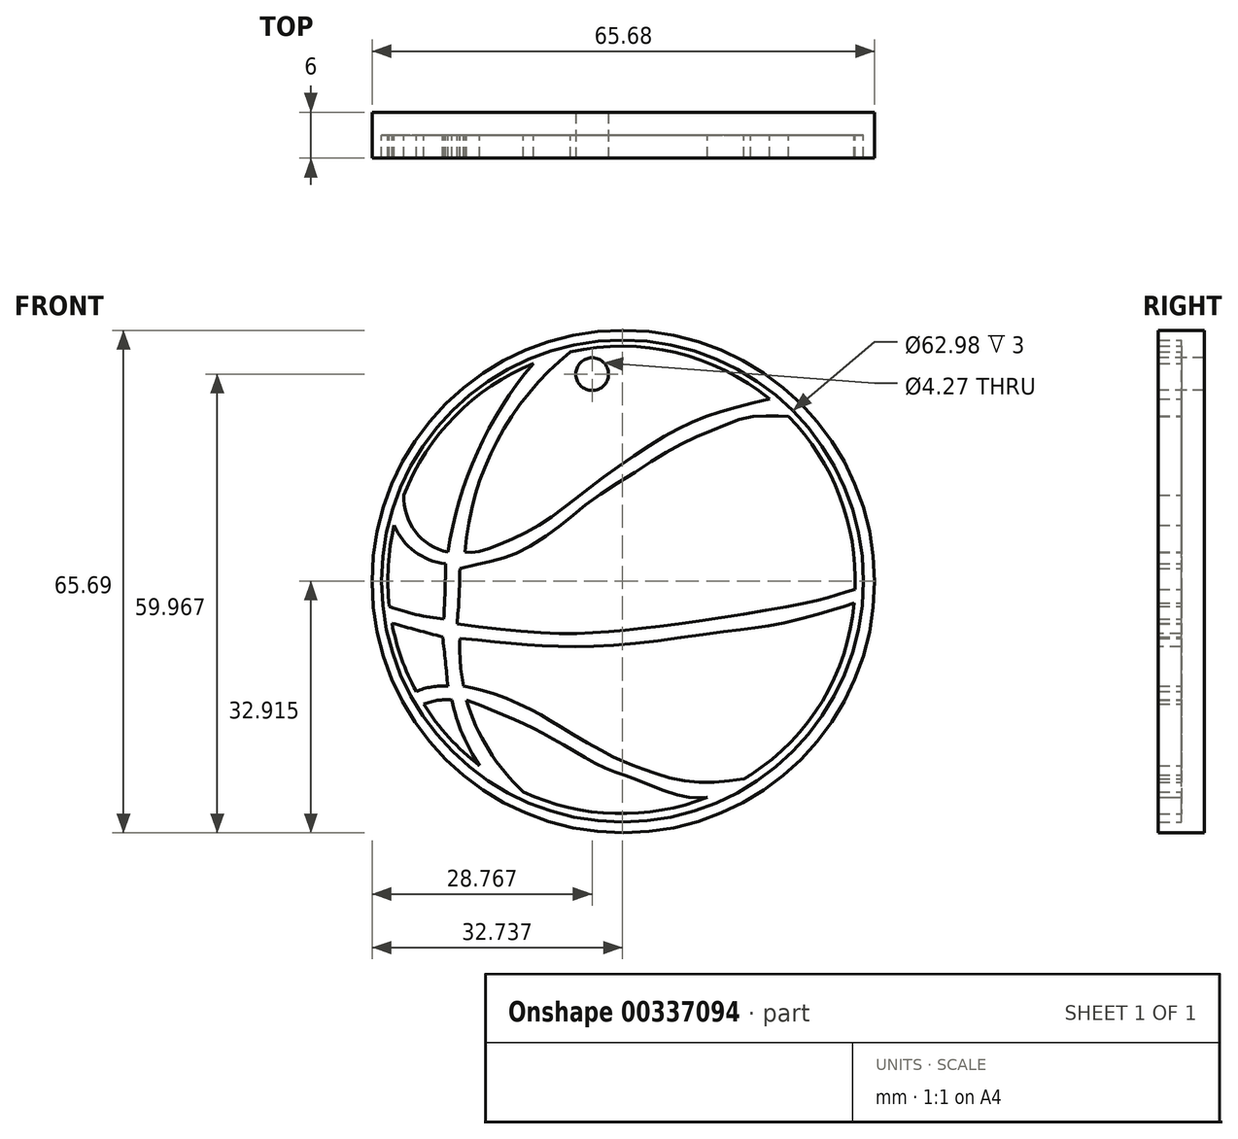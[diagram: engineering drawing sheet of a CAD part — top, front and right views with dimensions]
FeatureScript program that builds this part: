
annotation { "Feature Type Name" : "Feature", "Feature Type Description" : "" }
export const myFeature = defineFeature(function(context is Context, id is Id, definition is map)
    precondition{}
    {
        {
            var Q0;
            Q0=qCreatedBy(makeId("Front.planeOp"),FACE);
            var sketch = newSketch(context, id + "F0", { "sketchPlane" : qUnion([Q0])});
            skCircle(sketch, "E0", {"center": v(1.45, 1.07) * mm, "radius": 31.49 * mm});
            skPoint(sketch, "E0.first.point", {"position": v(-24.62, -16.6) * mm});
            skPoint(sketch, "E0.second.point", {"position": v(30.66, 12.8) * mm});
            skPoint(sketch, "E0.third.point", {"position": v(-14.09, 28.45) * mm});
            skFitSpline(sketch, "E1", {"points": [v(-19.8, -6.45) * mm, v(-12.36, -7.12) * mm, v(-6.04, -7.5) * mm, v(4.04, -6.97) * mm, v(15.92, -5.4) * mm, v(21.41, -4.64) * mm, v(28.48, -2.84) * mm, v(31.72, -1.78) * mm], "startDerivative": vector(52.87, -4.89) * mm, "endDerivative": vector(28.74, 9.86) * mm});
            skArc(sketch, "E2", {"start": v(-28.38, 8.36) * mm, "mid": v(-29.17, 3.08) * mm, "end": v(-29.03, -2.26) * mm});
            skPoint(sketch, "E2.first.point", {"position": v(-29.13, -1.18) * mm});
            skPoint(sketch, "E2.second.point", {"position": v(17.43, 27.18) * mm});
            skPoint(sketch, "E2.third.point", {"position": v(18.18, -24.27) * mm});
            skFitSpline(sketch, "E3", {"points": [v(31.85, 0) * mm, v(29.23, -0.8) * mm, v(25.1, -1.86) * mm, v(11.7, -4.11) * mm, v(1.18, -5.4) * mm, v(-7.17, -5.77) * mm, v(-20.18, -4.57) * mm], "startDerivative": vector(-26.82, -8.38) * mm, "endDerivative": vector(-65.54, 7.8) * mm});
            skArc(sketch, "E4", {"start": v(-27.14, 12.31) * mm, "mid": v(-25.62, 7.53) * mm, "end": v(-21.39, 4.84) * mm});
            skArc(sketch, "E5", {"start": v(-28.38, 8.36) * mm, "mid": v(-25.73, 4.91) * mm, "end": v(-21.69, 3.33) * mm});
            skArc(sketch, "E6", {"start": v(-21.39, -12.69) * mm, "mid": v(-23.5, -12.78) * mm, "end": v(-25.52, -13.37) * mm});
            skArc(sketch, "E7", {"start": v(-20.86, -14.5) * mm, "mid": v(-22.74, -14.53) * mm, "end": v(-24.54, -15.04) * mm});
            skArc(sketch, "E8", {"start": v(-28.7, -4.45) * mm, "mid": v(-25.39, -5.36) * mm, "end": v(-22.06, -6.22) * mm});
            skArc(sketch, "E9", {"start": v(-29.03, -2.26) * mm, "mid": v(-25.53, -3.32) * mm, "end": v(-21.91, -3.89) * mm});
            skArc(sketch, "E10", {"start": v(-10.2, 29.5) * mm, "mid": v(-17.52, 17.95) * mm, "end": v(-21.39, 4.84) * mm});
            skArc(sketch, "E11", {"start": v(-21.91, -3.89) * mm, "mid": v(-21.76, -0.28) * mm, "end": v(-21.69, 3.33) * mm});
            skArc(sketch, "E12", {"start": v(-21.39, -12.69) * mm, "mid": v(-21.7, -9.45) * mm, "end": v(-22.06, -6.22) * mm});
            skArc(sketch, "E13", {"start": v(-20.86, -14.5) * mm, "mid": v(-19.46, -18.96) * mm, "end": v(-17.23, -23.06) * mm});
            skArc(sketch, "E14", {"start": v(-18.98, -14.5) * mm, "mid": v(-16.05, -21) * mm, "end": v(-11.5, -26.52) * mm});
            skArc(sketch, "E15", {"start": v(-19.8, -6.45) * mm, "mid": v(-19.75, -9.58) * mm, "end": v(-19.35, -12.69) * mm});
            skArc(sketch, "E16", {"start": v(-20.18, -4.57) * mm, "mid": v(-19.92, -0.92) * mm, "end": v(-19.8, 2.73) * mm});
            skArc(sketch, "E17", {"start": v(-5.37, 31.02) * mm, "mid": v(-14.96, 19.36) * mm, "end": v(-19.16, 4.86) * mm});
            skFitSpline(sketch, "E18", {"points": [v(-19.16, 4.86) * mm, v(-17.73, 4.86) * mm, v(-14.42, 5.94) * mm, v(-8.7, 8.89) * mm, v(-2.61, 13.45) * mm, v(5.88, 19.35) * mm, v(12.6, 22.66) * mm, v(20.7, 24.84) * mm], "startDerivative": vector(18.93, -1.68) * mm, "endDerivative": vector(50.1, 11.47) * mm});
            skFitSpline(sketch, "E19", {"points": [v(23.16, 22.58) * mm, v(20.9, 22.66) * mm, v(17.6, 22.4) * mm, v(13.66, 20.96) * mm, v(8.83, 18.82) * mm, v(3.56, 15.6) * mm, v(-2.88, 11.4) * mm, v(-6.82, 8.17) * mm, v(-12.1, 4.86) * mm, v(-15.14, 3.79) * mm, v(-19.8, 2.73) * mm], "startDerivative": vector(-30.82, 1.74) * mm, "endDerivative": vector(-49.79, -10.77) * mm});
            skFitSpline(sketch, "E20", {"points": [v(-19.35, -12.69) * mm, v(-15.94, -13.47) * mm, v(-10.58, -15.71) * mm, v(-6.73, -17.95) * mm, v(0, -21.8) * mm, v(3.56, -23.31) * mm, v(9.9, -25.1) * mm, v(17.32, -24.82) * mm], "startDerivative": vector(27.74, -4.94) * mm, "endDerivative": vector(44.65, 5.64) * mm});
            skFitSpline(sketch, "E21", {"points": [v(-18.98, -14.5) * mm, v(-16.93, -15.26) * mm, v(-12.45, -17.14) * mm, v(-9.14, -18.75) * mm, v(-4.85, -21.17) * mm, v(-0.83, -23.4) * mm, v(3.1, -24.83) * mm, v(9.37, -27.07) * mm, v(12.57, -27.2) * mm], "startDerivative": vector(20.02, -7.25) * mm, "endDerivative": vector(26.35, 2.3) * mm});
            skArc(sketch, "E22.trimOffspring", {"start": v(-28.7, -4.45) * mm, "mid": v(-27.46, -9.03) * mm, "end": v(-25.52, -13.37) * mm});
            skArc(sketch, "E23.trimOffspring", {"start": v(-24.54, -15.04) * mm, "mid": v(-21.24, -19.38) * mm, "end": v(-17.23, -23.06) * mm});
            skArc(sketch, "E24.trimOffspring", {"start": v(-11.5, -26.52) * mm, "mid": v(0.46, -29.33) * mm, "end": v(12.57, -27.2) * mm});
            skArc(sketch, "E25.trimOffspring", {"start": v(17.32, -24.82) * mm, "mid": v(17.75, -24.55) * mm, "end": v(18.18, -24.27) * mm});
            skArc(sketch, "E26.trimOffspring", {"start": v(20.7, 24.84) * mm, "mid": v(8.38, 30.94) * mm, "end": v(-5.37, 31.02) * mm});
            skArc(sketch, "E27.trimOffspring", {"start": v(-10.2, 29.5) * mm, "mid": v(-20.44, 22.65) * mm, "end": v(-27.14, 12.31) * mm});
            skArc(sketch, "E28.trimOffspring", {"start": v(31.85, 0) * mm, "mid": v(29.84, 12.19) * mm, "end": v(23.16, 22.58) * mm});
            skFitSpline(sketch, "E29", {"points": [v(31.72, -1.78) * mm, v(33.97, -1.04) * mm], "startDerivative": vector(2.25, 0.74) * mm, "endDerivative": vector(2.25, 0.74) * mm});
            skArc(sketch, "E30", {"start": v(18.18, -24.27) * mm, "mid": v(27.58, -14.6) * mm, "end": v(31.72, -1.78) * mm});
            skCircle(sketch, "E31", {"center": v(1.55, 1) * mm, "radius": 32.84 * mm});
            skPoint(sketch, "E31.first.point", {"position": v(-29.62, -9.36) * mm});
            skPoint(sketch, "E31.second.point", {"position": v(24.95, 24.04) * mm});
            skPoint(sketch, "E31.third.point", {"position": v(25.6, -21.38) * mm});
            skSolve(sketch);
        }
        {
            var Q0;
            Q0=makeQuery(id+"F0.imprint","IMPRINT",FACE,{"disambiguationData":[TD([[makeQuery(id+"F0.imprint","IMPRINT",EDGE,{"derivedFrom":sQuery(id+"F0.wireOp",EDGE,"E3")}),-1.0]])]});
            var Q1;
            Q1=makeQuery(id+"F0.imprint","IMPRINT",FACE,{"disambiguationData":[TD([[makeQuery(id+"F0.imprint","IMPRINT",EDGE,{"derivedFrom":sQuery(id+"F0.wireOp",EDGE,"E17")}),1.0]])]});
            var Q2;
            Q2=makeQuery(id+"F0.imprint","IMPRINT",FACE,{"disambiguationData":[TD([[makeQuery(id+"F0.imprint","IMPRINT",EDGE,{"derivedFrom":sQuery(id+"F0.wireOp",EDGE,"E0")}),1.0]])]});
            var Q3;
            Q3=makeQuery(id+"F0.imprint","IMPRINT",FACE,{"disambiguationData":[TD([[makeQuery(id+"F0.imprint","IMPRINT",EDGE,{"derivedFrom":sQuery(id+"F0.wireOp",EDGE,"E1")}),-1.0]])]});
            var Q4;
            Q4=makeQuery(id+"F0.imprint","IMPRINT",FACE,{"disambiguationData":[TD([[makeQuery(id+"F0.imprint","IMPRINT",EDGE,{"derivedFrom":sQuery(id+"F0.wireOp",EDGE,"E6")}),-1.0]])]});
            var Q5;
            Q5=makeQuery(id+"F0.imprint","IMPRINT",FACE,{"disambiguationData":[TD([[makeQuery(id+"F0.imprint","IMPRINT",EDGE,{"derivedFrom":sQuery(id+"F0.wireOp",EDGE,"E14")}),1.0]])]});
            var Q6;
            Q6=makeQuery(id+"F0.imprint","IMPRINT",FACE,{"disambiguationData":[TD([[makeQuery(id+"F0.imprint","IMPRINT",EDGE,{"derivedFrom":sQuery(id+"F0.wireOp",EDGE,"E2")}),1.0]])]});
            var Q7;
            Q7=makeQuery(id+"F0.imprint","IMPRINT",FACE,{"disambiguationData":[TD([[makeQuery(id+"F0.imprint","IMPRINT",EDGE,{"derivedFrom":sQuery(id+"F0.wireOp",EDGE,"E4")}),1.0]])]});
            var Q8;
            Q8=makeQuery(id+"F0.imprint","IMPRINT",FACE,{"disambiguationData":[TD([[makeQuery(id+"F0.imprint","IMPRINT",EDGE,{"derivedFrom":sQuery(id+"F0.wireOp",EDGE,"E7")}),1.0]])]});
            var Q9;
            Q9=makeQuery(id+"F0.imprint","IMPRINT",FACE,{"disambiguationData":[TD([[makeQuery(id+"F0.imprint","IMPRINT",EDGE,{"derivedFrom":sQuery(id+"F0.wireOp",EDGE,"E0")}),-1.0]])]});
            extrude(context, id + "F1", {"entities" : qUnion([Q0, Q1, Q2, Q3, Q4, Q5, Q6, Q7, Q8, Q9]), "depth" : 3 * mm});
        }
        {
            var Q0;
            Q0=makeQuery(id+"F0.imprint","IMPRINT",FACE,{"disambiguationData":[TD([[makeQuery(id+"F0.imprint","IMPRINT",EDGE,{"derivedFrom":sQuery(id+"F0.wireOp",EDGE,"E17")}),1.0]])]});
            var Q1;
            Q1=makeQuery(id+"F0.imprint","IMPRINT",FACE,{"disambiguationData":[TD([[makeQuery(id+"F0.imprint","IMPRINT",EDGE,{"derivedFrom":sQuery(id+"F0.wireOp",EDGE,"E4")}),1.0]])]});
            var Q2;
            Q2=makeQuery(id+"F0.imprint","IMPRINT",FACE,{"disambiguationData":[TD([[makeQuery(id+"F0.imprint","IMPRINT",EDGE,{"derivedFrom":sQuery(id+"F0.wireOp",EDGE,"E3")}),-1.0]])]});
            var Q3;
            Q3=makeQuery(id+"F0.imprint","IMPRINT",FACE,{"disambiguationData":[TD([[makeQuery(id+"F0.imprint","IMPRINT",EDGE,{"derivedFrom":sQuery(id+"F0.wireOp",EDGE,"E2")}),1.0]])]});
            var Q4;
            Q4=makeQuery(id+"F0.imprint","IMPRINT",FACE,{"disambiguationData":[TD([[makeQuery(id+"F0.imprint","IMPRINT",EDGE,{"derivedFrom":sQuery(id+"F0.wireOp",EDGE,"E1")}),-1.0]])]});
            var Q5;
            Q5=makeQuery(id+"F0.imprint","IMPRINT",FACE,{"disambiguationData":[TD([[makeQuery(id+"F0.imprint","IMPRINT",EDGE,{"derivedFrom":sQuery(id+"F0.wireOp",EDGE,"E14")}),1.0]])]});
            var Q6;
            Q6=makeQuery(id+"F0.imprint","IMPRINT",FACE,{"disambiguationData":[TD([[makeQuery(id+"F0.imprint","IMPRINT",EDGE,{"derivedFrom":sQuery(id+"F0.wireOp",EDGE,"E7")}),1.0]])]});
            var Q7;
            Q7=makeQuery(id+"F0.imprint","IMPRINT",FACE,{"disambiguationData":[TD([[makeQuery(id+"F0.imprint","IMPRINT",EDGE,{"derivedFrom":sQuery(id+"F0.wireOp",EDGE,"E6")}),-1.0]])]});
            var Q8;
            Q8=makeQuery(id+"F0.imprint","IMPRINT",FACE,{"disambiguationData":[TD([[makeQuery(id+"F0.imprint","IMPRINT",EDGE,{"derivedFrom":sQuery(id+"F0.wireOp",EDGE,"E0")}),-1.0]])]});
            extrude(context, id + "F2", {"entities" : qUnion([Q0, Q1, Q2, Q3, Q4, Q5, Q6, Q7, Q8]), "operationType" : NewBodyOperationType.ADD, "depth" : 6 * mm});
        }
        {
            var Q0;
            Q0=makeQuery(id+"F2.opExtrude","CAP_FACE",FACE,{"disambiguationData":[OSD([sQuery(id+"F0.wireOp",EDGE,"E17"),sQuery(id+"F0.wireOp",EDGE,"E18"),sQuery(id+"F0.wireOp",EDGE,"E26.trimOffspring")])],"isStart":false});
            var sketch = newSketch(context, id + "F3", { "sketchPlane" : qUnion([Q0])});
            skCircle(sketch, "E32", {"center": v(-2.52, 28.12) * mm, "radius": 2.14 * mm});
            skSolve(sketch);
        }
        {
            var Q0;
            Q0=makeQuery(id+"F3.imprint","IMPRINT",FACE,{"disambiguationData":[TD([[makeQuery(id+"F3.imprint","IMPRINT",EDGE,{"derivedFrom":sQuery(id+"F3.wireOp",EDGE,"E32")}),1.0]])]});
            extrude(context, id + "F4", {"entities" : qUnion([Q0]), "operationType" : NewBodyOperationType.REMOVE, "oppositeDirection" : true, "depth" : 25 * mm});
        }
    });
